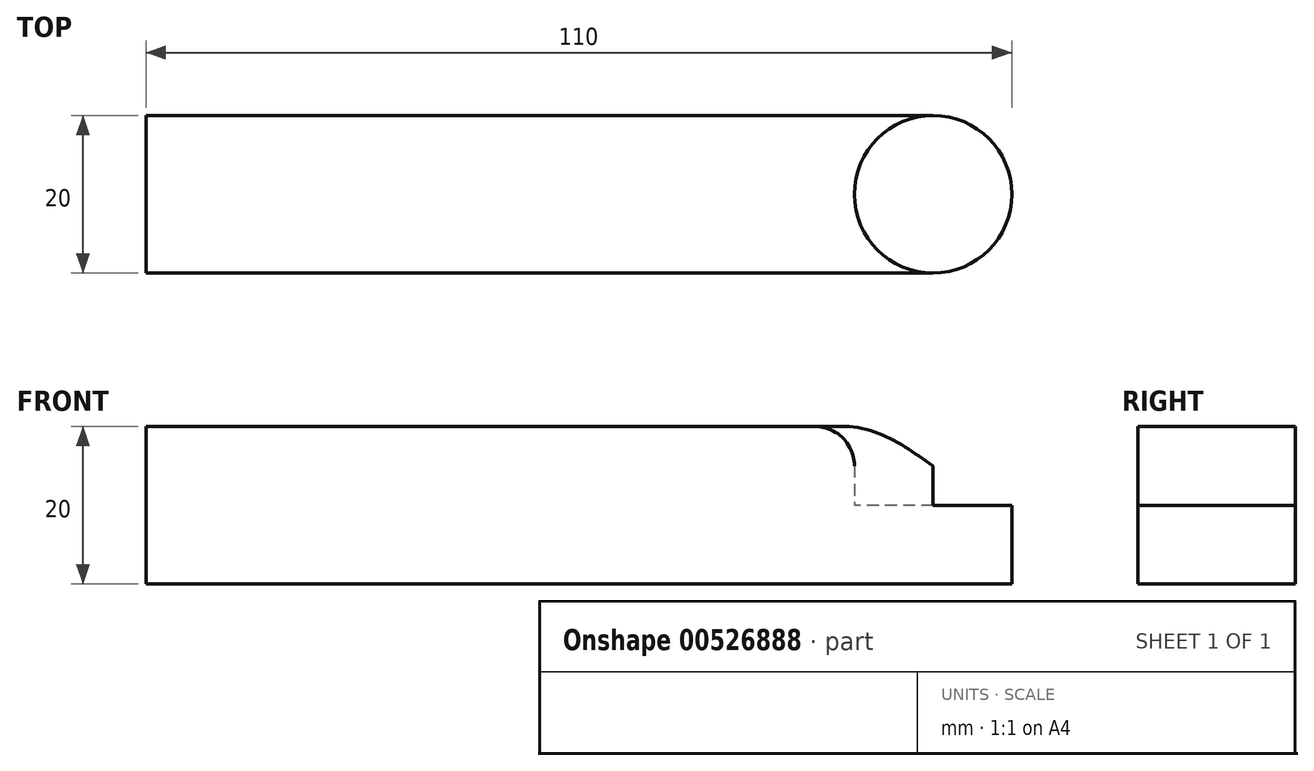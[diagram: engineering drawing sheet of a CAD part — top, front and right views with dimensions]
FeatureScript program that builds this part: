
annotation { "Feature Type Name" : "Feature", "Feature Type Description" : "" }
export const myFeature = defineFeature(function(context is Context, id is Id, definition is map)
    precondition{}
    {
        {
            assignVariable(context, id + "F0", {"name" : "instance", "anyValue" : 0});
        }
        {
            assignVariable(context, id + "F1", {"name" : "thickness", "anyValue" : [20, 35, 50][getVariable(context, 'instance')]});
        }
        {
            var Q0;
            Q0=qCreatedBy(makeId("Top.planeOp"),FACE);
            var sketch = newSketch(context, id + "F2", { "sketchPlane" : qUnion([Q0])});
            skLineSegment(sketch, "E0.bottom", {"start": v(0, 0) * mm, "end": v(100, 0) * mm});
            skLineSegment(sketch, "E0.top", {"start": v(0, -20) * mm, "end": v(100, -20) * mm});
            skLineSegment(sketch, "E0.left", {"start": v(0, 0) * mm, "end": v(0, -20) * mm});
            skLineSegment(sketch, "E0.right", {"start": v(100, 0) * mm, "end": v(100, -20) * mm});
            skCircle(sketch, "E1", {"center": v(100, -10) * mm, "radius": 10 * mm});
            skSolve(sketch);
        }
        {
            var Q0;
            {var subQ0=sQuery(id+"F2.wireOp",EDGE,"E0.bottom");Q0=makeQuery(id+"F2.imprint","IMPRINT",FACE,{"disambiguationData":[TD([[makeQuery(id+"F2.imprint","IMPRINT",EDGE,{"derivedFrom":subQ0}),-1.0]])]});}
            extrude(context, id + "F3", {"entities" : qUnion([Q0]), "endBound" : BoundingType.SYMMETRIC, "depth" : (getVariable(context, 'thickness')) * mm, "offsetDistance" : 25 * mm});
        }
        {
            var Q0;
            {var subQ0=sQuery(id+"F2.wireOp",EDGE,"E0.right");Q0=makeQuery(id+"F2.imprint","IMPRINT",FACE,{"disambiguationData":[TD([[makeQuery(id+"F2.imprint","IMPRINT",EDGE,{"derivedFrom":subQ0}),-1.0]])]});}
            var Q1;
            {var subQ0=sQuery(id+"F2.wireOp",EDGE,"E0.right");Q1=makeQuery(id+"F2.imprint","IMPRINT",FACE,{"disambiguationData":[TD([[makeQuery(id+"F2.imprint","IMPRINT",EDGE,{"derivedFrom":subQ0}),1.0]])]});}
            extrude(context, id + "F4", {"entities" : qUnion([Q0, Q1]), "operationType" : NewBodyOperationType.ADD, "oppositeDirection" : true, "depth" : 10 * mm, "offsetDistance" : 25 * mm});
        }
        {
            var Q0;
            Q0=makeQuery(id+"F3.opExtrude","CAP_EDGE",EDGE,{"disambiguationData":[OSD([sQuery(id+"F2.wireOp",EDGE,"E1")])],"isStart":false});
            fillet(context, id + "F5", {"entities" : qUnion([Q0]), "radius" : 5 * mm, "tangentPropagation" : true, "allowEdgeOverflow" : false});
        }
    });
